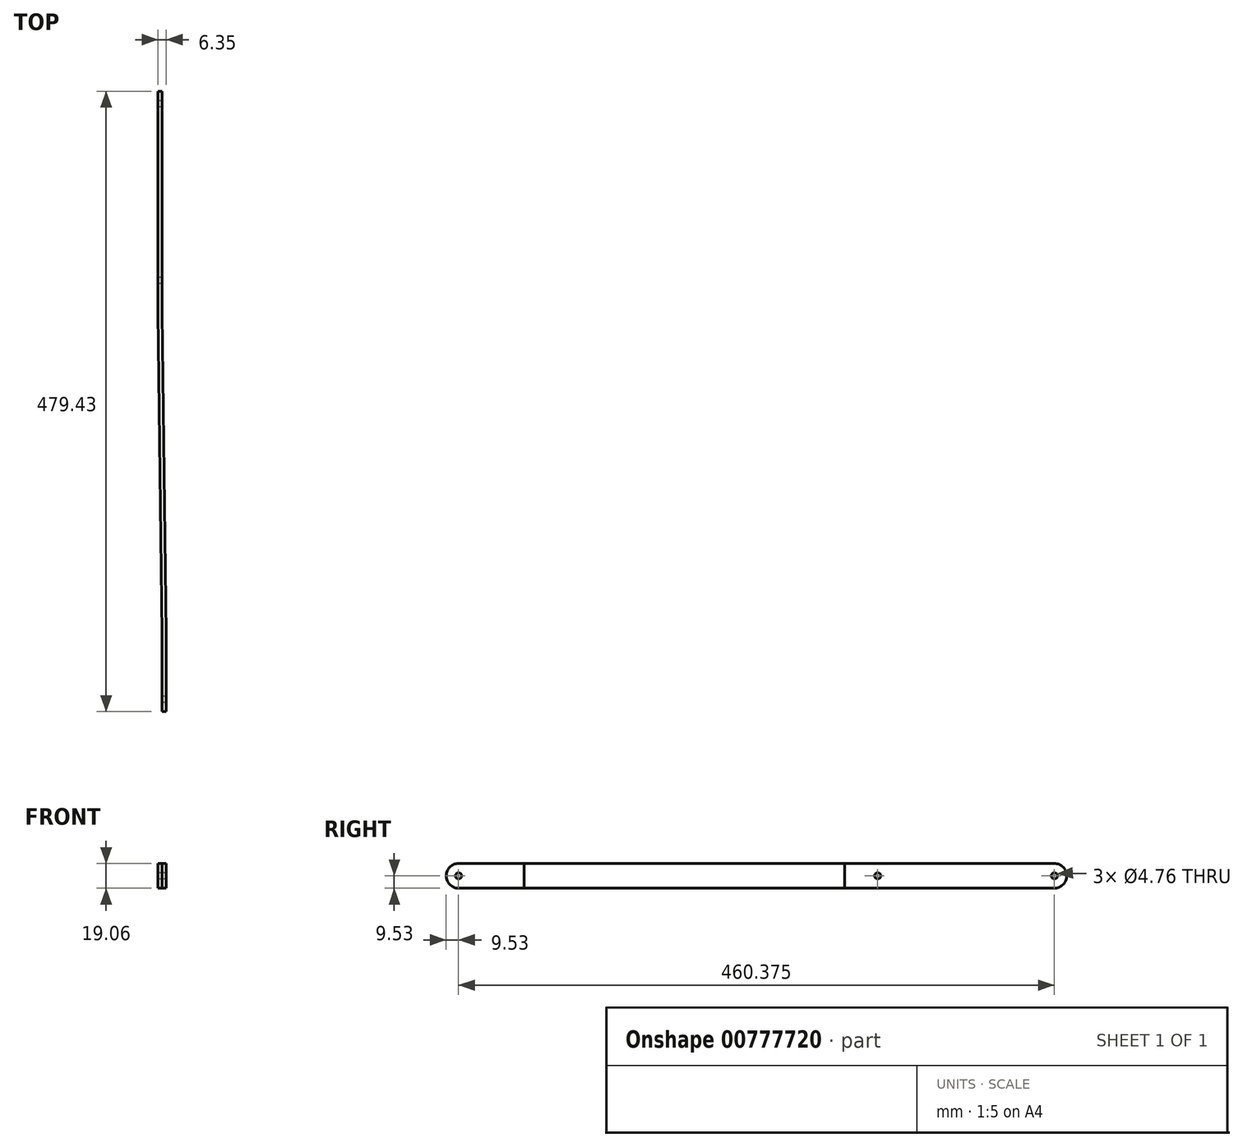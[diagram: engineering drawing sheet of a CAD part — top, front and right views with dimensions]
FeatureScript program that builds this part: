
annotation { "Feature Type Name" : "Feature", "Feature Type Description" : "" }
export const myFeature = defineFeature(function(context is Context, id is Id, definition is map)
    precondition{}
    {
        {
            var Q0;
            Q0=qCreatedBy(makeId("Right.planeOp"),FACE);
            var sketch = newSketch(context, id + "F0", { "sketchPlane" : qUnion([Q0])});
            skLineSegment(sketch, "E0.bottom", {"start": v(0, 9.53) * mm, "end": v(460.38, 9.53) * mm});
            skLineSegment(sketch, "E0.top", {"start": v(0, -9.52) * mm, "end": v(460.38, -9.52) * mm});
            skArc(sketch, "E1.filletArc", {"start": v(0, 9.53) * mm, "mid": v(-9.53, 0) * mm, "end": v(0, -9.53) * mm});
            skArc(sketch, "E2.filletArc", {"start": v(460.38, -9.52) * mm, "mid": v(469.9, 0) * mm, "end": v(460.38, 9.53) * mm});
            skCircle(sketch, "E3", {"center": v(0, 0) * mm, "radius": 2.38 * mm});
            skCircle(sketch, "E4", {"center": v(460.38, 0) * mm, "radius": 2.38 * mm});
            skCircle(sketch, "E5", {"center": v(323.85, 0) * mm, "radius": 2.38 * mm});
            skSolve(sketch);
        }
        {
            var Q0;
            Q0=qSketchRegion(id+"F0",true);
            extrude(context, id + "F1", {"entities" : qUnion([Q0]), "depth" : 6.35 * mm, "offsetDistance" : 25.4 * mm});
        }
        {
            var Q0;
            Q0=makeQuery(id+"F1.opExtrude","SWEPT_FACE",FACE,{"disambiguationData":[OSD([sQuery(id+"F0.wireOp",EDGE,"E0.bottom")])]});
            var sketch = newSketch(context, id + "F2", { "sketchPlane" : qUnion([Q0])});
            skPoint(sketch, "E6.oppositeSnap0", {"position": v(3.18, 460.38) * mm});
            skLineSegment(sketch, "E6.bottom", {"start": v(6.35, 50.8) * mm, "end": v(3.18, 298.47) * mm});
            skLineSegment(sketch, "E6.top", {"start": v(6.35, 469.9) * mm, "end": v(3.18, 469.9) * mm});
            skLineSegment(sketch, "E6.left", {"start": v(6.35, 50.8) * mm, "end": v(6.35, 469.9) * mm});
            skLineSegment(sketch, "E6.right", {"start": v(3.18, 298.47) * mm, "end": v(3.18, 469.9) * mm});
            skPoint(sketch, "E7.oppositeSnap0", {"position": v(3.18, 0) * mm});
            skLineSegment(sketch, "E7.bottom", {"start": v(0, 298.45) * mm, "end": v(3.18, 50.78) * mm});
            skLineSegment(sketch, "E7.top", {"start": v(0, -9.53) * mm, "end": v(3.18, -9.53) * mm});
            skLineSegment(sketch, "E7.left", {"start": v(0, 298.45) * mm, "end": v(0, -9.52) * mm});
            skLineSegment(sketch, "E7.right", {"start": v(3.18, 50.78) * mm, "end": v(3.18, -9.52) * mm});
            skSolve(sketch);
        }
        {
            var Q0;
            Q0 = qSketchRegion(id + "F2", true);
            extrude(context, id + "F3", {"entities" : qUnion([Q0]), "operationType" : NewBodyOperationType.REMOVE, "oppositeDirection" : true, "depth" : 25.4 * mm, "offsetDistance" : 25.4 * mm});
        }
    });
